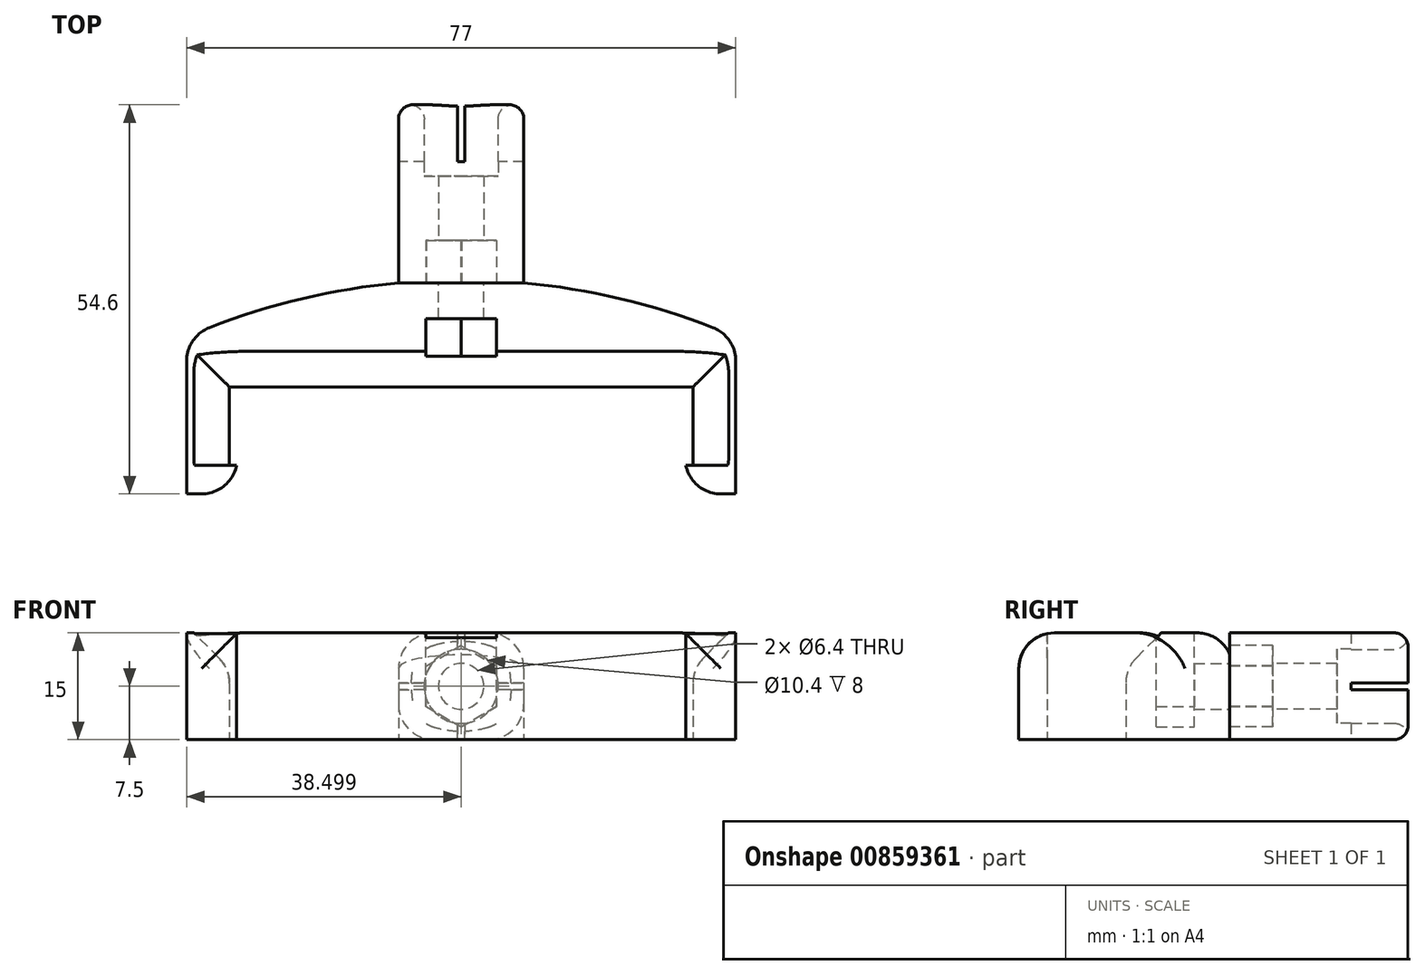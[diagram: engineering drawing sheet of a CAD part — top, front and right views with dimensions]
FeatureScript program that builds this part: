
annotation { "Feature Type Name" : "Feature", "Feature Type Description" : "" }
export const myFeature = defineFeature(function(context is Context, id is Id, definition is map)
    precondition{}
    {
        {
            var Q0;
            Q0=qCreatedBy(makeId("Top.planeOp"),FACE);
            var sketch = newSketch(context, id + "F0", { "sketchPlane" : qUnion([Q0])});
            skLineSegment(sketch, "E0.bottom", {"start": v(-68.8, 23.62) * mm, "end": v(8.2, 23.62) * mm});
            skLineSegment(sketch, "E0.top", {"start": v(-68.8, 1.62) * mm, "end": v(8.2, 1.62) * mm});
            skLineSegment(sketch, "E0.left", {"start": v(-68.8, 23.62) * mm, "end": v(-68.8, 1.62) * mm});
            skLineSegment(sketch, "E0.right", {"start": v(8.2, 23.62) * mm, "end": v(8.2, 1.62) * mm});
            skLineSegment(sketch, "E1.bottom", {"start": v(-62.8, 1.62) * mm, "end": v(2.2, 1.62) * mm});
            skLineSegment(sketch, "E1.top", {"start": v(-62.8, 16.62) * mm, "end": v(2.2, 16.62) * mm});
            skLineSegment(sketch, "E1.left", {"start": v(-62.8, 1.62) * mm, "end": v(-62.8, 16.62) * mm});
            skLineSegment(sketch, "E1.right", {"start": v(2.2, 1.62) * mm, "end": v(2.2, 16.62) * mm});
            skLineSegment(sketch, "E2", {"start": v(-30.3, 23.62) * mm, "end": v(-30.3, 1.62) * mm, "construction": true});
            skLineSegment(sketch, "E3.bottom", {"start": v(-62.8, 5.62) * mm, "end": v(-61.8, 5.62) * mm});
            skLineSegment(sketch, "E3.top", {"start": v(-62.8, 1.62) * mm, "end": v(-61.8, 1.62) * mm});
            skLineSegment(sketch, "E3.left", {"start": v(-62.8, 5.62) * mm, "end": v(-62.8, 1.62) * mm});
            skLineSegment(sketch, "E3.right", {"start": v(-61.8, 5.62) * mm, "end": v(-61.8, 1.62) * mm});
            skLineSegment(sketch, "E4", {"start": v(-62.8, 9.12) * mm, "end": v(-68.8, 9.12) * mm, "construction": true});
            skLineSegment(sketch, "E5", {"start": v(2.2, 9.12) * mm, "end": v(8.2, 9.12) * mm, "construction": true});
            skArc(sketch, "E6", {"start": v(8.2, 23.62) * mm, "mid": v(-30.3, 31.62) * mm, "end": v(-68.8, 23.62) * mm});
            skLineSegment(sketch, "E7", {"start": v(-30.3, 23.62) * mm, "end": v(-30.3, 31.62) * mm, "construction": true});
            skLineSegment(sketch, "E8", {"start": v(-39.09, 31.22) * mm, "end": v(-21.52, 31.22) * mm});
            skLineSegment(sketch, "E9.MirrorCS", {"start": v(2.2, 5.62) * mm, "end": v(2.2, 1.62) * mm});
            skLineSegment(sketch, "E10.MirrorCS", {"start": v(2.2, 1.62) * mm, "end": v(-62.8, 1.62) * mm});
            skLineSegment(sketch, "E11.MirrorCS", {"start": v(1.2, 5.62) * mm, "end": v(1.2, 1.62) * mm});
            skLineSegment(sketch, "E12.MirrorCS", {"start": v(2.2, 5.62) * mm, "end": v(1.2, 5.62) * mm});
            skSolve(sketch);
        }
        {
            var Q0;
            {var subQ3=sQuery(id+"F0.wireOp",EDGE,"E11.MirrorCS");Q0=makeQuery(id+"F0.imprint","IMPRINT",FACE,{"disambiguationData":[TD([[makeQuery(id+"F0.imprint","IMPRINT",EDGE,{"derivedFrom":subQ3}),1.0]])]});}
            var Q1;
            Q1=makeQuery(id+"F0.imprint","IMPRINT",FACE,{"disambiguationData":[TD([[makeQuery(id+"F0.imprint","IMPRINT",EDGE,{"derivedFrom":sQuery(id+"F0.wireOp",EDGE,"E0.bottom")}),-1.0]])]});
            var Q2;
            {var subQ0=sQuery(id+"F0.wireOp",EDGE,"E0.bottom");Q2=makeQuery(id+"F0.imprint","IMPRINT",FACE,{"disambiguationData":[TD([[makeQuery(id+"F0.imprint","IMPRINT",EDGE,{"derivedFrom":subQ0}),1.0]])]});}
            var Q3;
            {var subQ4=sQuery(id+"F0.wireOp",EDGE,"E3.bottom");Q3=makeQuery(id+"F0.imprint","IMPRINT",FACE,{"disambiguationData":[TD([[makeQuery(id+"F0.imprint","IMPRINT",EDGE,{"derivedFrom":subQ4}),-1.0]])]});}
            extrude(context, id + "F1", {"entities" : qUnion([Q0, Q1, Q2, Q3]), "depth" : 15 * mm, "offsetDistance" : 25 * mm});
        }
        {
            var Q0;
            Q0=makeQuery(id+"F1.opExtrude","SWEPT_FACE",FACE,{"disambiguationData":[OSD([sQuery(id+"F0.wireOp",EDGE,"E8")])]});
            var sketch = newSketch(context, id + "F2", { "sketchPlane" : qUnion([Q0])});
            skLineSegment(sketch, "E13", {"start": v(39.09, 7.5) * mm, "end": v(21.52, 7.5) * mm, "construction": true});
            skCircle(sketch, "E14", {"center": v(30.3, 7.5) * mm, "radius": 3.2 * mm});
            skSolve(sketch);
        }
        {
            var Q0;
            Q0=makeQuery(id+"F2.imprint","IMPRINT",FACE,{"disambiguationData":[TD([[makeQuery(id+"F2.imprint","IMPRINT",EDGE,{"derivedFrom":sQuery(id+"F2.wireOp",EDGE,"E14")}),1.0]])]});
            extrude(context, id + "F3", {"entities" : qUnion([Q0]), "operationType" : NewBodyOperationType.REMOVE, "oppositeDirection" : true, "depth" : 5 * mm, "offsetDistance" : 25 * mm});
        }
        {
            var Q0;
            Q0=makeQuery(id+"F3.boolean.opBoolean","COPY",FACE,{"derivedFrom":makeQuery(id+"F3.opExtrude","CAP_FACE",FACE,{"disambiguationData":[OSD([sQuery(id+"F2.wireOp",EDGE,"E14")])],"isStart":false})});
            var sketch = newSketch(context, id + "F4", { "sketchPlane" : qUnion([Q0])});
            skCircle(sketch, "E15.cCircle", {"center": v(30.3, 7.5) * mm, "radius": 4.95 * mm, "construction": true});
            skLineSegment(sketch, "E15.0", {"start": v(30.3, 13.22) * mm, "end": v(35.25, 10.36) * mm});
            skLineSegment(sketch, "E15.1", {"start": v(35.25, 10.36) * mm, "end": v(35.25, 4.64) * mm});
            skLineSegment(sketch, "E15.2", {"start": v(35.25, 4.64) * mm, "end": v(30.3, 1.78) * mm});
            skLineSegment(sketch, "E15.3", {"start": v(30.3, 1.78) * mm, "end": v(25.35, 4.64) * mm});
            skLineSegment(sketch, "E15.4", {"start": v(25.35, 4.64) * mm, "end": v(25.35, 10.36) * mm});
            skLineSegment(sketch, "E15.5", {"start": v(25.35, 10.36) * mm, "end": v(30.3, 13.22) * mm});
            skPoint(sketch, "E15.0.midPoint", {"position": v(32.78, 11.79) * mm});
            skLineSegment(sketch, "E16.bottom", {"start": v(25.35, 10.36) * mm, "end": v(35.25, 10.36) * mm});
            skLineSegment(sketch, "E16.top", {"start": v(25.35, 15) * mm, "end": v(35.25, 15) * mm});
            skLineSegment(sketch, "E16.left", {"start": v(25.35, 10.36) * mm, "end": v(25.35, 15) * mm});
            skLineSegment(sketch, "E16.right", {"start": v(35.25, 10.36) * mm, "end": v(35.25, 15) * mm});
            skSolve(sketch);
        }
        {
            var Q0;
            Q0 = qSketchRegion(id + "F4", true);
            extrude(context, id + "F5", {"entities" : qUnion([Q0]), "operationType" : NewBodyOperationType.REMOVE, "oppositeDirection" : true, "depth" : 5.3 * mm, "offsetDistance" : 25 * mm});
        }
        {
            var Q0;
            Q0=makeQuery(id+"F1.opExtrude","SWEPT_FACE",FACE,{"disambiguationData":[OSD([sQuery(id+"F0.wireOp",EDGE,"E8")])]});
            extrude(context, id + "F6", {"entities" : qUnion([Q0]), "depth" : 15 * mm, "offsetDistance" : 25 * mm});
        }
        {
            var Q0;
            Q0=makeQuery(id+"F6.opExtrude","CAP_FACE",FACE,{"disambiguationData":[OSD([sQuery(id+"F0.wireOp",EDGE,"E8")])],"isStart":true});
            var sketch = newSketch(context, id + "F7", { "sketchPlane" : qUnion([Q0])});
            skCircle(sketch, "E17.cCircle", {"center": v(-30.3, 7.5) * mm, "radius": 4.95 * mm, "construction": true});
            skLineSegment(sketch, "E17.0", {"start": v(-30.35, 13.22) * mm, "end": v(-25.38, 10.4) * mm});
            skLineSegment(sketch, "E17.1", {"start": v(-25.38, 10.4) * mm, "end": v(-25.33, 4.69) * mm});
            skLineSegment(sketch, "E17.2", {"start": v(-25.33, 4.69) * mm, "end": v(-30.25, 1.78) * mm});
            skLineSegment(sketch, "E17.3", {"start": v(-30.25, 1.78) * mm, "end": v(-35.23, 4.6) * mm});
            skLineSegment(sketch, "E17.4", {"start": v(-35.23, 4.6) * mm, "end": v(-35.28, 10.31) * mm});
            skLineSegment(sketch, "E17.5", {"start": v(-35.28, 10.31) * mm, "end": v(-30.35, 13.22) * mm});
            skPoint(sketch, "E17.0.midPoint", {"position": v(-27.86, 11.8) * mm});
            skSolve(sketch);
        }
        {
            var Q0;
            Q0=makeQuery(id+"F7.imprint","IMPRINT",FACE,{"disambiguationData":[TD([[makeQuery(id+"F7.imprint","IMPRINT",EDGE,{"derivedFrom":sQuery(id+"F7.wireOp",EDGE,"E17.0")}),-1.0]])]});
            extrude(context, id + "F8", {"entities" : qUnion([Q0]), "operationType" : NewBodyOperationType.REMOVE, "oppositeDirection" : true, "depth" : 6 * mm, "offsetDistance" : 25 * mm});
        }
        {
            var Q0;
            {var subQ0=sQuery(id+"F0.wireOp",EDGE,"E8");var subQ1=sQuery(id+"F0.wireOp",EDGE,"E6");Q0=makeQuery(id+"F6.opExtrude","SWEPT_EDGE",EDGE,{"disambiguationData":[OSD([subQ1,subQ0]),TDD([makeQuery(id+"F1.opExtrude","CAP_VERTEX",VERTEX,{"disambiguationData":[OSD([subQ1,subQ0]),TDD([makeQuery(id+"F0.imprint","INTERSECT",VERTEX,{"disambiguationData":[OD(0.0)],"derivedFrom":[subQ1,subQ0]})])],"isStart":false})])]});}
            var Q1;
            {var subQ0=sQuery(id+"F0.wireOp",EDGE,"E8");var subQ1=sQuery(id+"F0.wireOp",EDGE,"E6");Q1=makeQuery(id+"F6.opExtrude","SWEPT_EDGE",EDGE,{"disambiguationData":[OSD([subQ1,subQ0]),TDD([makeQuery(id+"F1.opExtrude","CAP_VERTEX",VERTEX,{"disambiguationData":[OSD([subQ1,subQ0]),TDD([makeQuery(id+"F0.imprint","INTERSECT",VERTEX,{"disambiguationData":[OD(0.0)],"derivedFrom":[subQ1,subQ0]})])],"isStart":true})])]});}
            var Q2;
            {var subQ0=sQuery(id+"F0.wireOp",EDGE,"E8");var subQ1=sQuery(id+"F0.wireOp",EDGE,"E6");Q2=makeQuery(id+"F6.opExtrude","SWEPT_EDGE",EDGE,{"disambiguationData":[OSD([subQ1,subQ0]),TDD([makeQuery(id+"F1.opExtrude","CAP_VERTEX",VERTEX,{"disambiguationData":[OSD([subQ1,subQ0]),TDD([makeQuery(id+"F0.imprint","INTERSECT",VERTEX,{"disambiguationData":[OD(1.0)],"derivedFrom":[subQ1,subQ0]})])],"isStart":false})])]});}
            var Q3;
            {var subQ0=sQuery(id+"F0.wireOp",EDGE,"E8");var subQ1=sQuery(id+"F0.wireOp",EDGE,"E6");Q3=makeQuery(id+"F6.opExtrude","SWEPT_EDGE",EDGE,{"disambiguationData":[OSD([subQ1,subQ0]),TDD([makeQuery(id+"F1.opExtrude","CAP_VERTEX",VERTEX,{"disambiguationData":[OSD([subQ1,subQ0]),TDD([makeQuery(id+"F0.imprint","INTERSECT",VERTEX,{"disambiguationData":[OD(1.0)],"derivedFrom":[subQ1,subQ0]})])],"isStart":true})])]});}
            fillet(context, id + "F9", {"entities" : qUnion([Q0, Q1, Q2, Q3]), "tangentPropagation" : true, "radius" : 5 * mm, "defaultsChanged" : false, "vertexSettings" : [], "allowEdgeOverflow" : false});
        }
        {
            var Q0;
            Q0=makeQuery(id+"F6.opExtrude","CAP_FACE",FACE,{"disambiguationData":[OSD([sQuery(id+"F0.wireOp",EDGE,"E8")])],"isStart":false});
            var sketch = newSketch(context, id + "F10", { "sketchPlane" : qUnion([Q0])});
            skCircle(sketch, "E18", {"center": v(30.3, 7.5) * mm, "radius": 5.2 * mm});
            skSolve(sketch);
        }
        {
            var Q0;
            Q0=makeQuery(id+"F10.imprint","IMPRINT",FACE,{"disambiguationData":[TD([[makeQuery(id+"F10.imprint","IMPRINT",EDGE,{"derivedFrom":sQuery(id+"F10.wireOp",EDGE,"E18")}),-1.0]])]});
            extrude(context, id + "F11", {"entities" : qUnion([Q0]), "operationType" : NewBodyOperationType.ADD, "depth" : 10 * mm, "offsetDistance" : 25 * mm});
        }
        {
            var Q0;
            Q0=makeQuery(id+"F11.opExtrude","CAP_FACE",FACE,{"disambiguationData":[OSD([sQuery(id+"F0.wireOp",EDGE,"E6"),sQuery(id+"F0.wireOp",EDGE,"E8"),sQuery(id+"F10.wireOp",EDGE,"E18")])],"isStart":false});
            var sketch = newSketch(context, id + "F12", { "sketchPlane" : qUnion([Q0])});
            skLineSegment(sketch, "E19.bottom", {"start": v(29.8, 15) * mm, "end": v(30.8, 15) * mm});
            skLineSegment(sketch, "E19.top", {"start": v(29.8, 0) * mm, "end": v(30.8, 0) * mm});
            skLineSegment(sketch, "E19.left", {"start": v(29.8, 15) * mm, "end": v(29.8, 0) * mm});
            skLineSegment(sketch, "E19.right", {"start": v(30.8, 15) * mm, "end": v(30.8, 0) * mm});
            skLineSegment(sketch, "E20.bottom", {"start": v(21.52, 8) * mm, "end": v(39.09, 8) * mm});
            skLineSegment(sketch, "E20.top", {"start": v(21.52, 7) * mm, "end": v(39.09, 7) * mm});
            skLineSegment(sketch, "E20.left", {"start": v(21.52, 8) * mm, "end": v(21.52, 7) * mm});
            skLineSegment(sketch, "E20.right", {"start": v(39.09, 8) * mm, "end": v(39.09, 7) * mm});
            skLineSegment(sketch, "E21", {"start": v(30.3, 15) * mm, "end": v(30.3, 0) * mm, "construction": true});
            skLineSegment(sketch, "E22", {"start": v(21.52, 7.5) * mm, "end": v(39.09, 7.5) * mm, "construction": true});
            skLineSegment(sketch, "E23", {"start": v(36.52, 7.5) * mm, "end": v(36.52, 8) * mm, "construction": true});
            skLineSegment(sketch, "E24", {"start": v(36.52, 7.5) * mm, "end": v(36.52, 7) * mm, "construction": true});
            skLineSegment(sketch, "E25", {"start": v(30.3, 12.11) * mm, "end": v(30.8, 12.11) * mm, "construction": true});
            skLineSegment(sketch, "E26", {"start": v(30.3, 12.11) * mm, "end": v(29.8, 12.11) * mm, "construction": true});
            skSolve(sketch);
        }
        {
            var Q0;
            {var subQ0=sQuery(id+"F12.wireOp",EDGE,"E19.bottom");Q0=makeQuery(id+"F12.imprint","IMPRINT",FACE,{"disambiguationData":[TD([[makeQuery(id+"F12.imprint","IMPRINT",EDGE,{"derivedFrom":subQ0}),1.0]])]});}
            var Q1;
            {var subQ0=sQuery(id+"F12.wireOp",EDGE,"E20.left");Q1=makeQuery(id+"F12.imprint","IMPRINT",FACE,{"disambiguationData":[TD([[makeQuery(id+"F12.imprint","IMPRINT",EDGE,{"derivedFrom":subQ0}),1.0]])]});}
            var Q2;
            {var subQ0=sQuery(id+"F12.wireOp",EDGE,"E20.right");Q2=makeQuery(id+"F12.imprint","IMPRINT",FACE,{"disambiguationData":[TD([[makeQuery(id+"F12.imprint","IMPRINT",EDGE,{"derivedFrom":subQ0}),-1.0]])]});}
            var Q3;
            {var subQ0=sQuery(id+"F12.wireOp",EDGE,"E19.top");Q3=makeQuery(id+"F12.imprint","IMPRINT",FACE,{"disambiguationData":[TD([[makeQuery(id+"F12.imprint","IMPRINT",EDGE,{"derivedFrom":subQ0}),-1.0]])]});}
            extrude(context, id + "F13", {"entities" : qUnion([Q0, Q1, Q2, Q3]), "operationType" : NewBodyOperationType.REMOVE, "oppositeDirection" : true, "depth" : 8 * mm, "offsetDistance" : 25 * mm});
        }
        {
            var Q0;
            {var subQ0=sQuery(id+"F0.wireOp",EDGE,"E8");var subQ1=sQuery(id+"F0.wireOp",EDGE,"E6");Q0=makeQuery(id+"F11.opExtrude","CAP_EDGE",EDGE,{"disambiguationData":[OSD([subQ1,subQ0]),TDD([makeQuery(id+"F10.imprint","IMPRINT",EDGE,{"derivedFrom":makeQuery(id+"F9.opFillet","BLEND_EDGE",EDGE,{"blendedFrom":[makeQuery(id+"F6.opExtrude","SWEPT_EDGE",EDGE,{"disambiguationData":[OSD([subQ1,subQ0]),TDD([makeQuery(id+"F1.opExtrude","CAP_VERTEX",VERTEX,{"disambiguationData":[OSD([subQ1,subQ0]),TDD([makeQuery(id+"F0.imprint","INTERSECT",VERTEX,{"disambiguationData":[OD(1.0)],"derivedFrom":[subQ1,subQ0]})])],"isStart":false})])]}),makeQuery(id+"F6.opExtrude","CAP_FACE",FACE,{"disambiguationData":[OSD([subQ0])],"isStart":false})],"blendedInto":[makeQuery(id+"F6.opExtrude","CAP_FACE",FACE,{"disambiguationData":[OSD([subQ0])],"isStart":false})]})})])],"isStart":false});}
            var Q1;
            {var subQ0=sQuery(id+"F0.wireOp",EDGE,"E8");var subQ1=sQuery(id+"F0.wireOp",EDGE,"E6");Q1=makeQuery(id+"F11.opExtrude","CAP_EDGE",EDGE,{"disambiguationData":[OSD([subQ1,subQ0]),TDD([makeQuery(id+"F10.imprint","IMPRINT",EDGE,{"derivedFrom":makeQuery(id+"F9.opFillet","BLEND_EDGE",EDGE,{"blendedFrom":[makeQuery(id+"F6.opExtrude","SWEPT_EDGE",EDGE,{"disambiguationData":[OSD([subQ1,subQ0]),TDD([makeQuery(id+"F1.opExtrude","CAP_VERTEX",VERTEX,{"disambiguationData":[OSD([subQ1,subQ0]),TDD([makeQuery(id+"F0.imprint","INTERSECT",VERTEX,{"disambiguationData":[OD(0.0)],"derivedFrom":[subQ1,subQ0]})])],"isStart":false})])]}),makeQuery(id+"F6.opExtrude","CAP_FACE",FACE,{"disambiguationData":[OSD([subQ0])],"isStart":false})],"blendedInto":[makeQuery(id+"F6.opExtrude","CAP_FACE",FACE,{"disambiguationData":[OSD([subQ0])],"isStart":false})]})})])],"isStart":false});}
            var Q2;
            {var subQ0=sQuery(id+"F0.wireOp",EDGE,"E8");var subQ1=sQuery(id+"F0.wireOp",EDGE,"E6");Q2=makeQuery(id+"F11.opExtrude","CAP_EDGE",EDGE,{"disambiguationData":[OSD([subQ1,subQ0]),TDD([makeQuery(id+"F10.imprint","IMPRINT",EDGE,{"derivedFrom":makeQuery(id+"F9.opFillet","BLEND_EDGE",EDGE,{"blendedFrom":[makeQuery(id+"F6.opExtrude","SWEPT_EDGE",EDGE,{"disambiguationData":[OSD([subQ1,subQ0]),TDD([makeQuery(id+"F1.opExtrude","CAP_VERTEX",VERTEX,{"disambiguationData":[OSD([subQ1,subQ0]),TDD([makeQuery(id+"F0.imprint","INTERSECT",VERTEX,{"disambiguationData":[OD(0.0)],"derivedFrom":[subQ1,subQ0]})])],"isStart":true})])]}),makeQuery(id+"F6.opExtrude","CAP_FACE",FACE,{"disambiguationData":[OSD([subQ0])],"isStart":false})],"blendedInto":[makeQuery(id+"F6.opExtrude","CAP_FACE",FACE,{"disambiguationData":[OSD([subQ0])],"isStart":false})]})})])],"isStart":false});}
            var Q3;
            {var subQ0=sQuery(id+"F0.wireOp",EDGE,"E8");var subQ1=sQuery(id+"F0.wireOp",EDGE,"E6");Q3=makeQuery(id+"F11.opExtrude","CAP_EDGE",EDGE,{"disambiguationData":[OSD([subQ1,subQ0]),TDD([makeQuery(id+"F10.imprint","IMPRINT",EDGE,{"derivedFrom":makeQuery(id+"F9.opFillet","BLEND_EDGE",EDGE,{"blendedFrom":[makeQuery(id+"F6.opExtrude","SWEPT_EDGE",EDGE,{"disambiguationData":[OSD([subQ1,subQ0]),TDD([makeQuery(id+"F1.opExtrude","CAP_VERTEX",VERTEX,{"disambiguationData":[OSD([subQ1,subQ0]),TDD([makeQuery(id+"F0.imprint","INTERSECT",VERTEX,{"disambiguationData":[OD(1.0)],"derivedFrom":[subQ1,subQ0]})])],"isStart":true})])]}),makeQuery(id+"F6.opExtrude","CAP_FACE",FACE,{"disambiguationData":[OSD([subQ0])],"isStart":false})],"blendedInto":[makeQuery(id+"F6.opExtrude","CAP_FACE",FACE,{"disambiguationData":[OSD([subQ0])],"isStart":false})]})})])],"isStart":false});}
            var Q4;
            {var subQ0=sQuery(id+"F10.wireOp",EDGE,"E18");var subQ3=sQuery(id+"F12.wireOp",EDGE,"E19.right");var subQ4=makeQuery(id+"F11.opExtrude","CAP_EDGE",EDGE,{"disambiguationData":[OSD([subQ0])],"isStart":false});Q4=makeQuery(id+"F13.boolean.opBoolean","SPLIT",EDGE,{"disambiguationData":[TD([makeQuery(id+"F13.opExtrude","SWEPT_FACE",FACE,{"disambiguationData":[OSD([subQ3]),TDD([makeQuery(id+"F12.imprint","IMPRINT",EDGE,{"disambiguationData":[TD([[makeQuery(id+"F12.imprint","INTERSECT",VERTEX,{"disambiguationData":[OD(1.0)],"derivedFrom":[subQ4,subQ3]}),-1.0]])],"derivedFrom":subQ3})])]})])],"derivedFrom":subQ4});}
            var Q5;
            {var subQ0=sQuery(id+"F10.wireOp",EDGE,"E18");var subQ3=sQuery(id+"F12.wireOp",EDGE,"E19.right");var subQ4=makeQuery(id+"F11.opExtrude","CAP_EDGE",EDGE,{"disambiguationData":[OSD([subQ0])],"isStart":false});Q5=makeQuery(id+"F13.boolean.opBoolean","SPLIT",EDGE,{"disambiguationData":[TD([makeQuery(id+"F13.opExtrude","SWEPT_FACE",FACE,{"disambiguationData":[OSD([subQ3]),TDD([makeQuery(id+"F12.imprint","IMPRINT",EDGE,{"disambiguationData":[TD([[makeQuery(id+"F12.imprint","INTERSECT",VERTEX,{"disambiguationData":[OD(0.0)],"derivedFrom":[subQ4,subQ3]}),1.0]])],"derivedFrom":subQ3})])]})])],"derivedFrom":subQ4});}
            var Q6;
            {var subQ0=sQuery(id+"F10.wireOp",EDGE,"E18");var subQ1=sQuery(id+"F12.wireOp",EDGE,"E19.left");var subQ3=makeQuery(id+"F11.opExtrude","CAP_EDGE",EDGE,{"disambiguationData":[OSD([subQ0])],"isStart":false});Q6=makeQuery(id+"F13.boolean.opBoolean","SPLIT",EDGE,{"disambiguationData":[TD([makeQuery(id+"F13.opExtrude","SWEPT_FACE",FACE,{"disambiguationData":[OSD([subQ1]),TDD([makeQuery(id+"F12.imprint","IMPRINT",EDGE,{"disambiguationData":[TD([[makeQuery(id+"F12.imprint","INTERSECT",VERTEX,{"disambiguationData":[OD(0.0)],"derivedFrom":[subQ3,subQ1]}),1.0]])],"derivedFrom":subQ1})])]})])],"derivedFrom":subQ3});}
            var Q7;
            {var subQ0=sQuery(id+"F10.wireOp",EDGE,"E18");var subQ4=makeQuery(id+"F11.opExtrude","CAP_EDGE",EDGE,{"disambiguationData":[OSD([subQ0])],"isStart":false});var subQ5=sQuery(id+"F12.wireOp",EDGE,"E19.left");Q7=makeQuery(id+"F13.boolean.opBoolean","SPLIT",EDGE,{"disambiguationData":[TD([makeQuery(id+"F13.opExtrude","SWEPT_FACE",FACE,{"disambiguationData":[OSD([subQ5]),TDD([makeQuery(id+"F12.imprint","IMPRINT",EDGE,{"disambiguationData":[TD([[makeQuery(id+"F12.imprint","INTERSECT",VERTEX,{"disambiguationData":[OD(1.0)],"derivedFrom":[subQ4,subQ5]}),-1.0]])],"derivedFrom":subQ5})])]})])],"derivedFrom":subQ4});}
            fillet(context, id + "F14", {"entities" : qUnion([Q0, Q1, Q2, Q3, Q4, Q5, Q6, Q7]), "tangentPropagation" : true, "radius" : 2 * mm, "defaultsChanged" : false, "vertexSettings" : [], "allowEdgeOverflow" : false});
        }
        {
            var Q0;
            Q0=makeQuery(id+"F1.opExtrude","CAP_EDGE",EDGE,{"disambiguationData":[OSD([sQuery(id+"F0.wireOp",EDGE,"E1.top")])],"isStart":false});
            var Q1;
            Q1=makeQuery(id+"F1.opExtrude","CAP_EDGE",EDGE,{"disambiguationData":[OSD([sQuery(id+"F0.wireOp",EDGE,"E1.right")])],"isStart":false});
            var Q2;
            Q2=makeQuery(id+"F1.opExtrude","CAP_EDGE",EDGE,{"disambiguationData":[OSD([sQuery(id+"F0.wireOp",EDGE,"E1.left")])],"isStart":false});
            chamfer(context, id + "F15", {"entities" : qUnion([Q0, Q1, Q2]), "width" : 5 * mm, "tangentPropagation" : true});
        }
        {
            var Q0;
            {var subQ0=sQuery(id+"F0.wireOp",EDGE,"E6");Q0=makeQuery(id+"F1.opExtrude","CAP_EDGE",EDGE,{"disambiguationData":[OSD([subQ0]),TDD([makeQuery(id+"F0.imprint","IMPRINT",EDGE,{"disambiguationData":[TD([[makeQuery(id+"F0.imprint","INTERSECT",VERTEX,{"disambiguationData":[OD(0.0)],"derivedFrom":[subQ0,sQuery(id+"F0.wireOp",EDGE,"E8")]}),-1.0]])],"derivedFrom":subQ0})])],"isStart":false});}
            var Q1;
            {var subQ0=sQuery(id+"F0.wireOp",EDGE,"E6");Q1=makeQuery(id+"F1.opExtrude","CAP_EDGE",EDGE,{"disambiguationData":[OSD([subQ0]),TDD([makeQuery(id+"F0.imprint","IMPRINT",EDGE,{"disambiguationData":[TD([[makeQuery(id+"F0.imprint","INTERSECT",VERTEX,{"disambiguationData":[OD(1.0)],"derivedFrom":[subQ0,sQuery(id+"F0.wireOp",EDGE,"E8")]}),1.0]])],"derivedFrom":subQ0})])],"isStart":false});}
            var Q2;
            {var subQ0=sQuery(id+"F0.wireOp",EDGE,"E0.top");var subQ1=makeQuery(id+"F0.imprint","INTERSECT",VERTEX,{"derivedFrom":[subQ0,sQuery(id+"F0.wireOp",EDGE,"E1.right")]});Q2=makeQuery(id+"F1.opExtrude","CAP_EDGE",EDGE,{"disambiguationData":[OSD([subQ0]),TDD([makeQuery(id+"F0.imprint","IMPRINT",EDGE,{"disambiguationData":[TD([[subQ1,-1.0]])],"derivedFrom":subQ0}),makeQuery(id+"F0.imprint","IMPRINT",EDGE,{"disambiguationData":[TD([[subQ1,1.0]])],"derivedFrom":subQ0})])],"isStart":false});}
            var Q3;
            Q3=makeQuery(id+"F1.opExtrude","SWEPT_EDGE",EDGE,{"disambiguationData":[OSD([sQuery(id+"F0.wireOp",EDGE,"E0.top"),sQuery(id+"F0.wireOp",EDGE,"E11.MirrorCS")])]});
            var Q4;
            {var subQ0=sQuery(id+"F0.wireOp",EDGE,"E0.top");Q4=makeQuery(id+"F1.opExtrude","CAP_EDGE",EDGE,{"disambiguationData":[OSD([subQ0]),TDD([makeQuery(id+"F0.imprint","IMPRINT",EDGE,{"disambiguationData":[TD([[makeQuery(id+"F0.imprint","INTERSECT",VERTEX,{"derivedFrom":[subQ0,sQuery(id+"F0.wireOp",EDGE,"E0.left")]}),-1.0]])],"derivedFrom":subQ0}),makeQuery(id+"F0.imprint","IMPRINT",EDGE,{"disambiguationData":[TD([[makeQuery(id+"F0.imprint","INTERSECT",VERTEX,{"derivedFrom":[subQ0,sQuery(id+"F0.wireOp",EDGE,"E3.right")]}),1.0]])],"derivedFrom":subQ0})])],"isStart":false});}
            var Q5;
            Q5=makeQuery(id+"F1.opExtrude","SWEPT_EDGE",EDGE,{"disambiguationData":[OSD([sQuery(id+"F0.wireOp",EDGE,"E0.top"),sQuery(id+"F0.wireOp",EDGE,"E3.right")])]});
            var Q6;
            {var subQ0=sQuery(id+"F0.wireOp",EDGE,"E1.top");Q6=makeQuery(id+"F15.opChamfer","BLEND_EDGE",EDGE,{"blendedFrom":[makeQuery(id+"F1.opExtrude","CAP_EDGE",EDGE,{"disambiguationData":[OSD([subQ0])],"isStart":false}),makeQuery(id+"F1.opExtrude","SWEPT_FACE",FACE,{"disambiguationData":[OSD([subQ0])]})],"blendedInto":[makeQuery(id+"F1.opExtrude","SWEPT_FACE",FACE,{"disambiguationData":[OSD([subQ0])]})]});}
            var Q7;
            {var subQ0=sQuery(id+"F0.wireOp",EDGE,"E1.right");Q7=makeQuery(id+"F15.opChamfer","BLEND_EDGE",EDGE,{"blendedFrom":[makeQuery(id+"F1.opExtrude","CAP_EDGE",EDGE,{"disambiguationData":[OSD([subQ0])],"isStart":false}),makeQuery(id+"F1.opExtrude","SWEPT_FACE",FACE,{"disambiguationData":[OSD([subQ0])]})],"blendedInto":[makeQuery(id+"F1.opExtrude","SWEPT_FACE",FACE,{"disambiguationData":[OSD([subQ0])]})]});}
            var Q8;
            {var subQ0=sQuery(id+"F0.wireOp",EDGE,"E1.left");Q8=makeQuery(id+"F15.opChamfer","BLEND_EDGE",EDGE,{"blendedFrom":[makeQuery(id+"F1.opExtrude","CAP_EDGE",EDGE,{"disambiguationData":[OSD([subQ0])],"isStart":false}),makeQuery(id+"F1.opExtrude","SWEPT_FACE",FACE,{"disambiguationData":[OSD([subQ0])]})],"blendedInto":[makeQuery(id+"F1.opExtrude","SWEPT_FACE",FACE,{"disambiguationData":[OSD([subQ0])]})]});}
            var Q9;
            Q9=makeQuery(id+"F1.opExtrude","SWEPT_EDGE",EDGE,{"disambiguationData":[OSD([sQuery(id+"F0.wireOp",EDGE,"E0.bottom"),sQuery(id+"F0.wireOp",EDGE,"E0.right"),sQuery(id+"F0.wireOp",EDGE,"E6")])]});
            var Q10;
            Q10=makeQuery(id+"F1.opExtrude","SWEPT_EDGE",EDGE,{"disambiguationData":[OSD([sQuery(id+"F0.wireOp",EDGE,"E0.bottom"),sQuery(id+"F0.wireOp",EDGE,"E0.left"),sQuery(id+"F0.wireOp",EDGE,"E6")])]});
            fillet(context, id + "F16", {"entities" : qUnion([Q0, Q1, Q2, Q3, Q4, Q5, Q6, Q7, Q8, Q9, Q10]), "tangentPropagation" : true, "radius" : 5 * mm, "defaultsChanged" : false, "vertexSettings" : [], "allowEdgeOverflow" : false});
        }
    });
